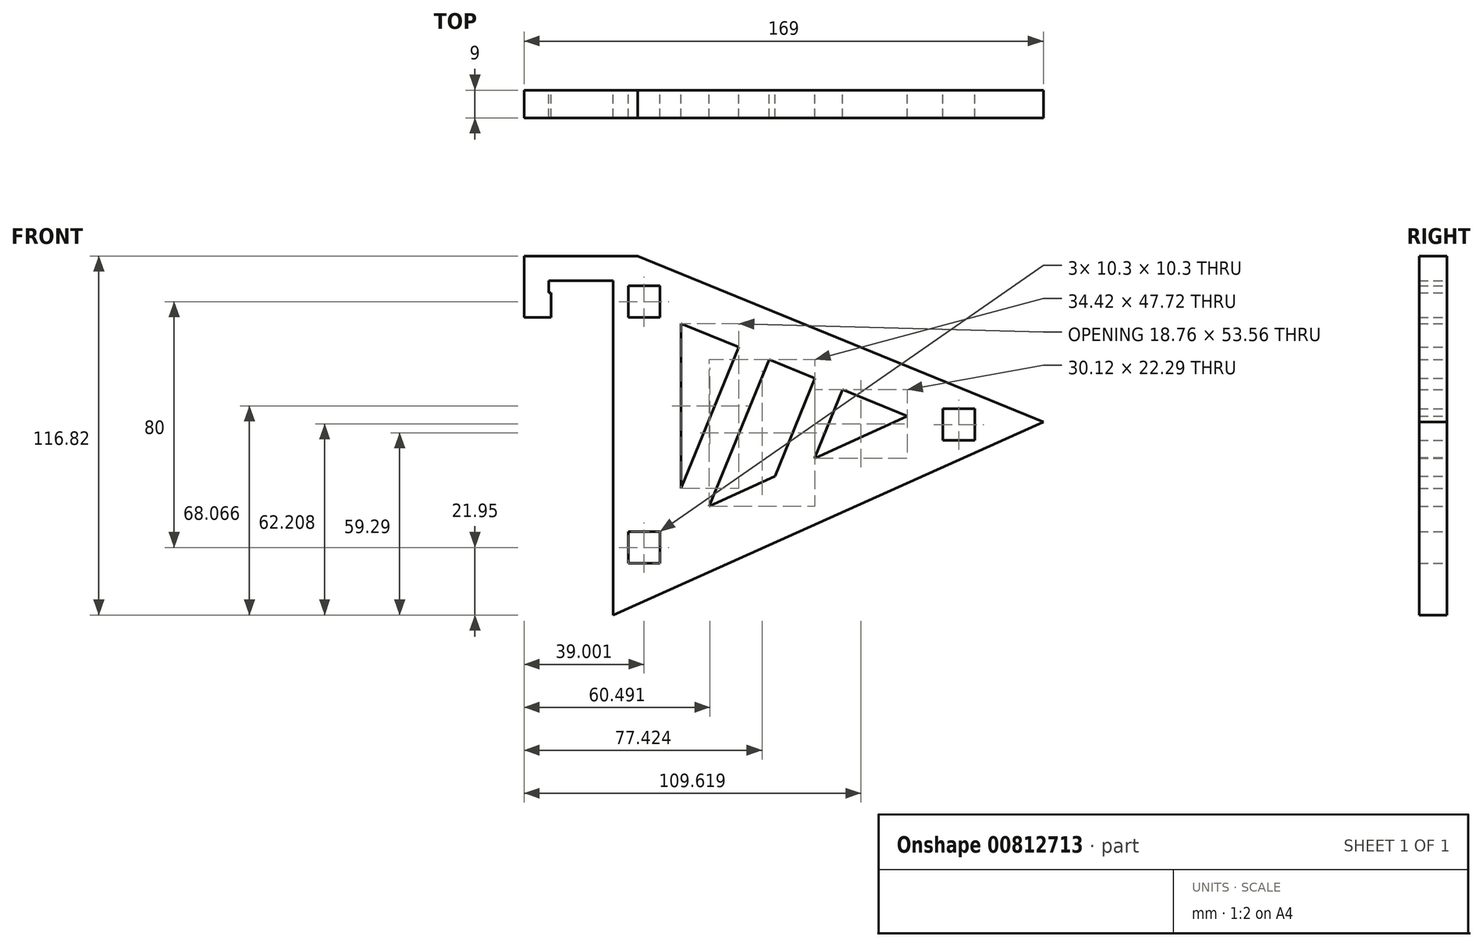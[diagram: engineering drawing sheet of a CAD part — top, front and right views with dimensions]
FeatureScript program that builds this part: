
annotation { "Feature Type Name" : "Feature", "Feature Type Description" : "" }
export const myFeature = defineFeature(function(context is Context, id is Id, definition is map)
    precondition{}
    {
        {
            var Q0;
            Q0=qCreatedBy(makeId("Front.planeOp"),FACE);
            var sketch = newSketch(context, id + "F0", { "sketchPlane" : qUnion([Q0])});
            skLineSegment(sketch, "E0", {"start": v(-30.75, 49.34) * mm, "end": v(-22.75, 49.34) * mm});
            skLineSegment(sketch, "E1", {"start": v(-30.75, 49.34) * mm, "end": v(-30.75, -60.3) * mm});
            skLineSegment(sketch, "E2", {"start": v(-22.75, 49.34) * mm, "end": v(109.25, -4.62) * mm});
            skLineSegment(sketch, "E3", {"start": v(-8.64, 27.36) * mm, "end": v(64.93, -2.7) * mm});
            skLineSegment(sketch, "E4", {"start": v(-8.64, -36.2) * mm, "end": v(-8.64, 27.36) * mm});
            skLineSegment(sketch, "E5", {"start": v(64.93, -2.7) * mm, "end": v(68.21, -1.22) * mm});
            skLineSegment(sketch, "E6", {"start": v(68.21, -1.22) * mm, "end": v(-8.64, -36.2) * mm});
            skLineSegment(sketch, "E7", {"start": v(10.12, 19.7) * mm, "end": v(-8.64, -26.2) * mm});
            skLineSegment(sketch, "E8", {"start": v(19.97, 15.67) * mm, "end": v(0.46, -32.05) * mm});
            skLineSegment(sketch, "E9", {"start": v(109.25, -4.62) * mm, "end": v(-30.75, -67.48) * mm});
            skLineSegment(sketch, "E10", {"start": v(-30.75, 41.34) * mm, "end": v(-51.75, 41.34) * mm});
            skLineSegment(sketch, "E11", {"start": v(-51.75, 41.34) * mm, "end": v(-51.75, 29.34) * mm});
            skLineSegment(sketch, "E12", {"start": v(-51.75, 29.34) * mm, "end": v(-59.75, 29.34) * mm});
            skLineSegment(sketch, "E13", {"start": v(-59.75, 29.34) * mm, "end": v(-59.75, 49.34) * mm});
            skLineSegment(sketch, "E14", {"start": v(-59.75, 49.34) * mm, "end": v(-30.75, 49.34) * mm});
            skLineSegment(sketch, "E15", {"start": v(-51.75, 37.34) * mm, "end": v(-51, 37.34) * mm});
            skLineSegment(sketch, "E16", {"start": v(-51.75, 29.34) * mm, "end": v(-51, 29.34) * mm});
            skLineSegment(sketch, "E17", {"start": v(-51, 37.34) * mm, "end": v(-51, 29.34) * mm});
            skLineSegment(sketch, "E18", {"start": v(34.88, 9.57) * mm, "end": v(21.85, -22.32) * mm});
            skLineSegment(sketch, "E19", {"start": v(43.93, 5.88) * mm, "end": v(41.12, -1) * mm});
            skLineSegment(sketch, "E20", {"start": v(41.12, -1) * mm, "end": v(34.88, -16.26) * mm});
            skLineSegment(sketch, "E21", {"start": v(34.88, -16.26) * mm, "end": v(34.8, -16.42) * mm});
            skLineSegment(sketch, "E22", {"start": v(-30.75, -60.3) * mm, "end": v(-30.75, -67.48) * mm});
            skLineSegment(sketch, "E23.bottom", {"start": v(-15.6, 29.32) * mm, "end": v(-25.9, 29.32) * mm});
            skLineSegment(sketch, "E23.top", {"start": v(-15.6, 39.62) * mm, "end": v(-25.9, 39.62) * mm});
            skLineSegment(sketch, "E23.left", {"start": v(-15.6, 29.32) * mm, "end": v(-15.6, 39.62) * mm});
            skLineSegment(sketch, "E23.right", {"start": v(-25.9, 29.32) * mm, "end": v(-25.9, 39.62) * mm});
            skPoint(sketch, "E23.middle", {"position": v(-20.75, 34.47) * mm});
            skLineSegment(sketch, "E24.bottom", {"start": v(-15.6, -50.68) * mm, "end": v(-25.9, -50.68) * mm});
            skLineSegment(sketch, "E24.top", {"start": v(-15.6, -40.38) * mm, "end": v(-25.9, -40.38) * mm});
            skLineSegment(sketch, "E24.left", {"start": v(-15.6, -50.68) * mm, "end": v(-15.6, -40.38) * mm});
            skLineSegment(sketch, "E24.right", {"start": v(-25.9, -50.68) * mm, "end": v(-25.9, -40.38) * mm});
            skPoint(sketch, "E24.middle", {"position": v(-20.75, -45.53) * mm});
            skLineSegment(sketch, "E25.bottom", {"start": v(86.87, -10.68) * mm, "end": v(76.57, -10.68) * mm});
            skLineSegment(sketch, "E25.top", {"start": v(86.87, -0.38) * mm, "end": v(76.57, -0.38) * mm});
            skLineSegment(sketch, "E25.left", {"start": v(86.87, -10.68) * mm, "end": v(86.87, -0.38) * mm});
            skLineSegment(sketch, "E25.right", {"start": v(76.57, -10.68) * mm, "end": v(76.57, -0.38) * mm});
            skPoint(sketch, "E25.middle", {"position": v(81.72, -5.53) * mm});
            skSolve(sketch);
        }
        {
            var Q0;
            {var subQ3=sQuery(id+"F0.wireOp",EDGE,"E10");Q0=makeQuery(id+"F0.imprint","IMPRINT",FACE,{"disambiguationData":[TD([[makeQuery(id+"F0.imprint","IMPRINT",EDGE,{"derivedFrom":subQ3}),-1.0]])]});}
            var Q1;
            {var subQ2=sQuery(id+"F0.wireOp",EDGE,"E15");Q1=makeQuery(id+"F0.imprint","IMPRINT",FACE,{"disambiguationData":[TD([[makeQuery(id+"F0.imprint","IMPRINT",EDGE,{"derivedFrom":subQ2}),-1.0]])]});}
            var Q2;
            {var subQ4=sQuery(id+"F0.wireOp",EDGE,"E7");Q2=makeQuery(id+"F0.imprint","IMPRINT",FACE,{"disambiguationData":[TD([[makeQuery(id+"F0.imprint","IMPRINT",EDGE,{"derivedFrom":subQ4}),1.0]])]});}
            var Q3;
            {var subQ0=sQuery(id+"F0.wireOp",EDGE,"E18");Q3=makeQuery(id+"F0.imprint","IMPRINT",FACE,{"disambiguationData":[TD([[makeQuery(id+"F0.imprint","IMPRINT",EDGE,{"derivedFrom":subQ0}),1.0]])]});}
            var Q4;
            {var subQ9=sQuery(id+"F0.wireOp",EDGE,"E0");Q4=makeQuery(id+"F0.imprint","IMPRINT",FACE,{"disambiguationData":[TD([[makeQuery(id+"F0.imprint","IMPRINT",EDGE,{"derivedFrom":subQ9}),-1.0]])]});}
            extrude(context, id + "F1", {"entities" : qUnion([Q0, Q1, Q2, Q3, Q4]), "depth" : 9 * mm, "offsetDistance" : 25.4 * mm});
        }
    });
